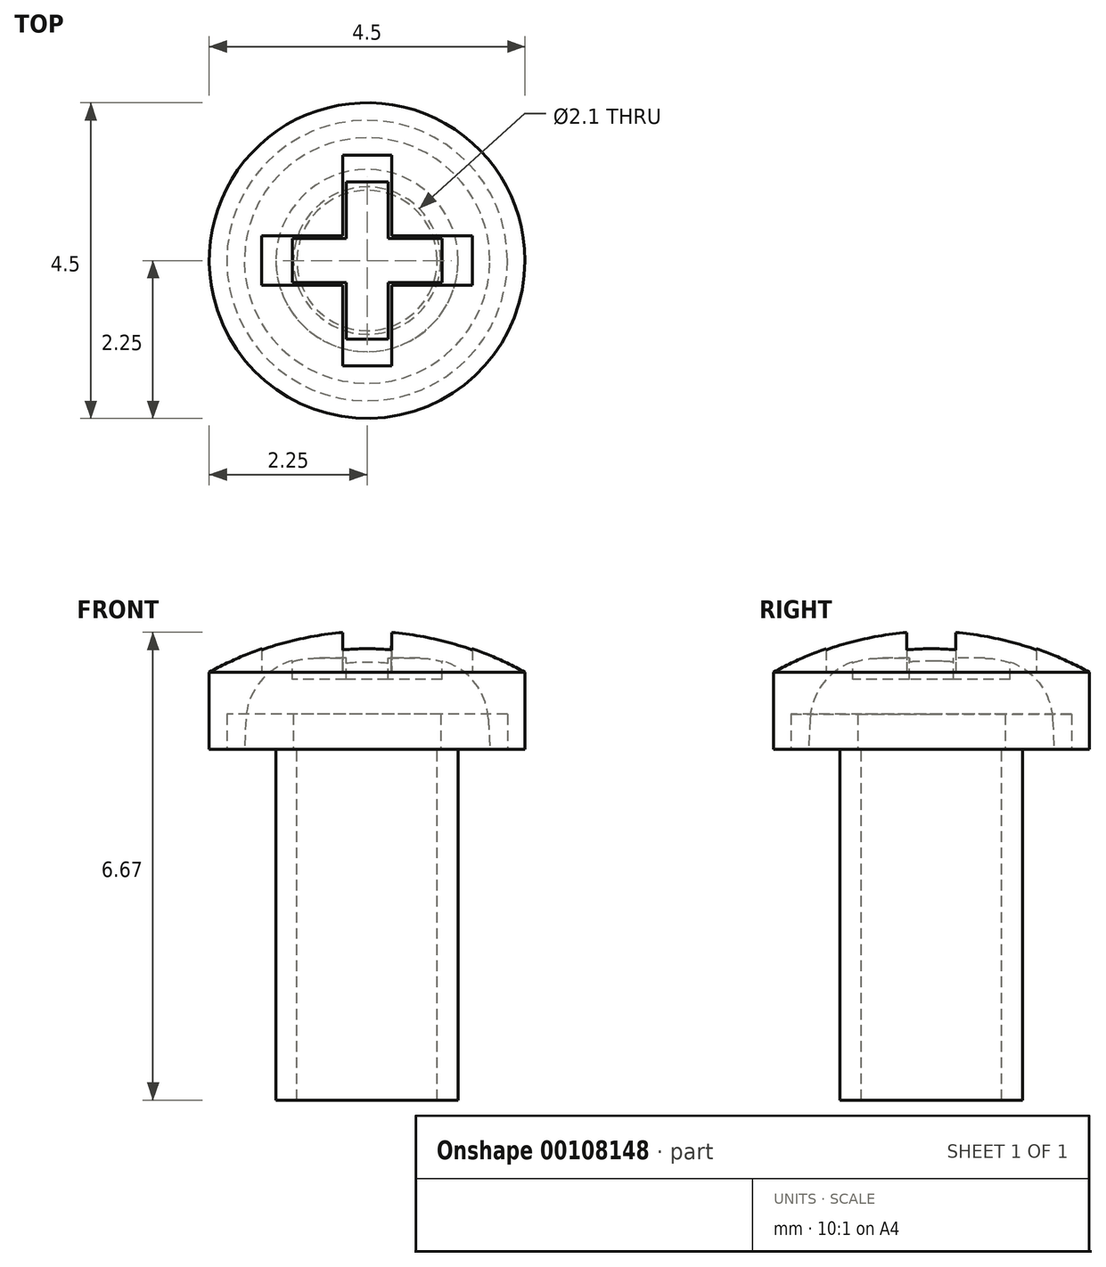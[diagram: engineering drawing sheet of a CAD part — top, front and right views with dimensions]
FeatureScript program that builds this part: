
annotation { "Feature Type Name" : "Feature", "Feature Type Description" : "" }
export const myFeature = defineFeature(function(context is Context, id is Id, definition is map)
    precondition{}
    {
        {
            var Q0;
            Q0=qCreatedBy(makeId("Front.planeOp"),FACE);
            var sketch = newSketch(context, id + "F0", { "sketchPlane" : qUnion([Q0])});
            skLineSegment(sketch, "E0", {"start": v(0, 1.5) * mm, "end": v(0, 0) * mm});
            skLineSegment(sketch, "E1", {"start": v(0, 0) * mm, "end": v(2, 0) * mm});
            skLineSegment(sketch, "E2", {"start": v(2, 0) * mm, "end": v(2, 0.7) * mm});
            skArc(sketch, "E3", {"start": v(2, 0.7) * mm, "mid": v(1.09, 1.31) * mm, "end": v(0, 1.5) * mm});
            skSolve(sketch);
        }
        {
            var Q0;
            Q0=qSketchRegion(id+"F0",true);
            var Q1;
            Q1=sQuery(id+"F0.wireOp",EDGE,"E0");
            revolve(context, id + "F1", {"entities" : qUnion([Q0]), "axis" : qUnion([Q1]), "revolveType" : RevolveType.FULL});
        }
        {
            var Q0;
            Q0=qCreatedBy(makeId("Top.planeOp"),FACE);
            cPlane(context, id + "F2", {"entities" : qUnion([Q0]), "cplaneType" : CPlaneType.OFFSET, "offset" : 1 * mm, "width" : 150 * mm, "height" : 150 * mm});
        }
        {
            var Q0;
            Q0=qCreatedBy(id+"F2.planeOp",FACE);
            var sketch = newSketch(context, id + "F3", { "sketchPlane" : qUnion([Q0])});
            skLineSegment(sketch, "E4.rect.bottom", {"start": v(0.34, 1.34) * mm, "end": v(-0.34, 1.34) * mm});
            skLineSegment(sketch, "E4.rect.top", {"start": v(0.34, -1.34) * mm, "end": v(-0.34, -1.34) * mm});
            skLineSegment(sketch, "E4.rect.left", {"start": v(0.34, 1.34) * mm, "end": v(0.34, -1.34) * mm});
            skLineSegment(sketch, "E4.rect.right", {"start": v(-0.34, 1.34) * mm, "end": v(-0.34, -1.34) * mm});
            skPoint(sketch, "E4.rect.middle", {"position": v(0, 0) * mm});
            skLineSegment(sketch, "E5.rect.bottom", {"start": v(1.32, 0.3) * mm, "end": v(-1.32, 0.3) * mm});
            skLineSegment(sketch, "E5.rect.top", {"start": v(1.32, -0.3) * mm, "end": v(-1.32, -0.3) * mm});
            skLineSegment(sketch, "E5.rect.left", {"start": v(1.32, 0.3) * mm, "end": v(1.32, -0.3) * mm});
            skLineSegment(sketch, "E5.rect.right", {"start": v(-1.32, 0.3) * mm, "end": v(-1.32, -0.3) * mm});
            skSolve(sketch);
        }
        {
            var Q0;
            Q0=qSketchRegion(id+"F3",true);
            extrude(context, id + "F4", {"entities" : qUnion([Q0]), "operationType" : NewBodyOperationType.REMOVE, "depth" : 25 * mm});
        }
        {
            var Q0;
            Q0=makeQuery(id+"F1.opRevolve","SWEPT_BODY",BODY,{"disambiguationData":[OSD([sQuery(id+"F0.wireOp",EDGE,"E0"),sQuery(id+"F0.wireOp",EDGE,"E1"),sQuery(id+"F0.wireOp",EDGE,"E2"),sQuery(id+"F0.wireOp",EDGE,"E3")])]});
            transform(context, id + "F5", {"entities" : qUnion([Q0]), "transformType" : TransformType.COPY});
        }
        {
            var Q0;
            Q0=makeQuery(id+"F1.opRevolve","SWEPT_FACE",FACE,{"disambiguationData":[OSD([sQuery(id+"F0.wireOp",EDGE,"E1")])]});
            var sketch = newSketch(context, id + "F6", { "sketchPlane" : qUnion([Q0])});
            skCircle(sketch, "E6", {"center": v(0, 0) * mm, "radius": 1.15 * mm});
            skSolve(sketch);
        }
        {
            var Q0;
            Q0=qSketchRegion(id+"F6",true);
            extrude(context, id + "F7", {"entities" : qUnion([Q0]), "operationType" : NewBodyOperationType.ADD, "depth" : 5 * mm});
        }
        {
            var Q0;
            Q0=qSketchRegion(id+"F6",true);
            extrude(context, id + "F8", {"entities" : qUnion([Q0]), "operationType" : NewBodyOperationType.ADD, "depth" : 4 * mm});
        }
        {
            var Q0;
            Q0=qCreatedBy(makeId("Front.planeOp"),FACE);
            var sketch = newSketch(context, id + "F9", { "sketchPlane" : qUnion([Q0])});
            skLineSegment(sketch, "E7", {"start": v(0, 0) * mm, "end": v(2.25, 0) * mm});
            skLineSegment(sketch, "E8", {"start": v(2.25, 0) * mm, "end": v(2.25, 1.1) * mm});
            skArc(sketch, "E9", {"start": v(2.25, 1.1) * mm, "mid": v(1.16, 1.54) * mm, "end": v(0, 1.7) * mm});
            skLineSegment(sketch, "E10", {"start": v(0, 1.7) * mm, "end": v(0, 0) * mm});
            skSolve(sketch);
        }
        {
            var Q0;
            Q0=qSketchRegion(id+"F9",true);
            var Q1;
            Q1=sQuery(id+"F9.wireOp",EDGE,"E10");
            revolve(context, id + "F10", {"entities" : qUnion([Q0]), "axis" : qUnion([Q1]), "revolveType" : RevolveType.FULL});
        }
        {
            var Q0;
            Q0=makeQuery(id+"F10.opRevolve","SWEPT_FACE",FACE,{"disambiguationData":[OSD([sQuery(id+"F9.wireOp",EDGE,"E7")])]});
            cPlane(context, id + "F11", {"entities" : qUnion([Q0]), "cplaneType" : CPlaneType.OFFSET, "offset" : 1.1 * mm, "oppositeDirection" : true, "width" : 150 * mm, "height" : 150 * mm});
        }
        {
            var Q0;
            Q0=qCreatedBy(id+"F11.planeOp",FACE);
            var sketch = newSketch(context, id + "F12", { "sketchPlane" : qUnion([Q0])});
            skLineSegment(sketch, "E11.rect.bottom", {"start": v(0.35, -1.5) * mm, "end": v(-0.35, -1.5) * mm});
            skLineSegment(sketch, "E11.rect.top", {"start": v(0.35, 1.5) * mm, "end": v(-0.35, 1.5) * mm});
            skLineSegment(sketch, "E11.rect.left", {"start": v(0.35, -1.5) * mm, "end": v(0.35, 1.5) * mm});
            skLineSegment(sketch, "E11.rect.right", {"start": v(-0.35, -1.5) * mm, "end": v(-0.35, 1.5) * mm});
            skPoint(sketch, "E11.rect.middle", {"position": v(0, 0) * mm});
            skLineSegment(sketch, "E12.rect.bottom", {"start": v(1.5, -0.35) * mm, "end": v(-1.5, -0.35) * mm});
            skLineSegment(sketch, "E12.rect.top", {"start": v(1.5, 0.35) * mm, "end": v(-1.5, 0.35) * mm});
            skLineSegment(sketch, "E12.rect.left", {"start": v(1.5, -0.35) * mm, "end": v(1.5, 0.35) * mm});
            skLineSegment(sketch, "E12.rect.right", {"start": v(-1.5, -0.35) * mm, "end": v(-1.5, 0.35) * mm});
            skSolve(sketch);
        }
        {
            var Q0;
            Q0=qSketchRegion(id+"F12",true);
            extrude(context, id + "F13", {"entities" : qUnion([Q0]), "operationType" : NewBodyOperationType.REMOVE, "oppositeDirection" : true, "depth" : 25 * mm});
        }
        {
            var Q0;
            Q0=makeQuery(id+"F10.opRevolve","SWEPT_BODY",BODY,{"disambiguationData":[OSD([sQuery(id+"F9.wireOp",EDGE,"E7"),sQuery(id+"F9.wireOp",EDGE,"E8"),sQuery(id+"F9.wireOp",EDGE,"E9"),sQuery(id+"F9.wireOp",EDGE,"E10")])]});
            transform(context, id + "F14", {"entities" : qUnion([Q0]), "transformType" : TransformType.COPY});
        }
        {
            var Q0;
            Q0=makeQuery(id+"F10.opRevolve","SWEPT_FACE",FACE,{"disambiguationData":[OSD([sQuery(id+"F9.wireOp",EDGE,"E7")])]});
            var sketch = newSketch(context, id + "F15", { "sketchPlane" : qUnion([Q0])});
            skCircle(sketch, "E13", {"center": v(0, 0) * mm, "radius": 1.3 * mm});
            skSolve(sketch);
        }
        {
            var Q0;
            Q0=qSketchRegion(id+"F15",true);
            extrude(context, id + "F16", {"entities" : qUnion([Q0]), "operationType" : NewBodyOperationType.ADD, "depth" : 4 * mm});
        }
        {
            var Q0;
            Q0=qSketchRegion(id+"F15",true);
            extrude(context, id + "F17", {"entities" : qUnion([Q0]), "operationType" : NewBodyOperationType.ADD, "depth" : 5 * mm});
        }
        {
            var Q0;
            Q0=qCreatedBy(makeId("Front.planeOp"),FACE);
            var sketch = newSketch(context, id + "F18", { "sketchPlane" : qUnion([Q0])});
            skLineSegment(sketch, "E14", {"start": v(0, 0) * mm, "end": v(1.75, 0) * mm});
            skLineSegment(sketch, "E15", {"start": v(0, 1.3) * mm, "end": v(0, 0) * mm});
            skLineSegment(sketch, "E16", {"start": v(0, 1.3) * mm, "end": v(0.82, 1.3) * mm});
            skLineSegment(sketch, "E17", {"start": v(1.75, 0) * mm, "end": v(1.73, 0.43) * mm});
            skArc(sketch, "E18", {"start": v(1.73, 0.43) * mm, "mid": v(1.45, 1.05) * mm, "end": v(0.82, 1.3) * mm});
            skLineSegment(sketch, "E19.bottom", {"start": v(0, 0) * mm, "end": v(1, 0) * mm});
            skLineSegment(sketch, "E19.top", {"start": v(0, -5) * mm, "end": v(1, -5) * mm});
            skLineSegment(sketch, "E19.left", {"start": v(0, 0) * mm, "end": v(0, -5) * mm});
            skLineSegment(sketch, "E19.right", {"start": v(1, 0) * mm, "end": v(1, -5) * mm});
            skSolve(sketch);
        }
        {
            var Q0;
            Q0=qSketchRegion(id+"F18",true);
            var Q1;
            Q1=sQuery(id+"F18.wireOp",EDGE,"E19.left");
            revolve(context, id + "F19", {"entities" : qUnion([Q0]), "axis" : qUnion([Q1]), "revolveType" : RevolveType.FULL});
        }
        {
            var Q0;
            Q0=makeQuery(id+"F19.opRevolve","SWEPT_FACE",FACE,{"disambiguationData":[OSD([sQuery(id+"F18.wireOp",EDGE,"E16")])]});
            var sketch = newSketch(context, id + "F20", { "sketchPlane" : qUnion([Q0])});
            skLineSegment(sketch, "E20.bottom", {"start": v(0.3, 1.12) * mm, "end": v(-0.3, 1.12) * mm});
            skLineSegment(sketch, "E20.top", {"start": v(0.3, -1.12) * mm, "end": v(-0.3, -1.12) * mm});
            skLineSegment(sketch, "E20.left", {"start": v(0.3, 1.12) * mm, "end": v(0.3, -1.12) * mm});
            skLineSegment(sketch, "E20.right", {"start": v(-0.3, 1.12) * mm, "end": v(-0.3, -1.12) * mm});
            skPoint(sketch, "E20.middle", {"position": v(0, 0) * mm});
            skLineSegment(sketch, "E21.bottom", {"start": v(1.07, 0.31) * mm, "end": v(-1.07, 0.31) * mm});
            skLineSegment(sketch, "E21.top", {"start": v(1.07, -0.31) * mm, "end": v(-1.07, -0.31) * mm});
            skLineSegment(sketch, "E21.left", {"start": v(1.07, 0.31) * mm, "end": v(1.07, -0.31) * mm});
            skLineSegment(sketch, "E21.right", {"start": v(-1.07, 0.31) * mm, "end": v(-1.07, -0.31) * mm});
            skSolve(sketch);
        }
        {
            var Q0;
            Q0=qSketchRegion(id+"F20",true);
            extrude(context, id + "F21", {"entities" : qUnion([Q0]), "operationType" : NewBodyOperationType.REMOVE, "oppositeDirection" : true, "depth" : 0.3 * mm});
        }
        {
            var Q0;
            Q0=qCreatedBy(makeId("Top.planeOp"),FACE);
            var sketch = newSketch(context, id + "F22", { "sketchPlane" : qUnion([Q0])});
            skCircle(sketch, "E22", {"center": v(0, 0) * mm, "radius": 2 * mm});
            skCircle(sketch, "E23", {"center": v(0, 0) * mm, "radius": 1.05 * mm});
            skSolve(sketch);
        }
        {
            var Q0;
            Q0=qSketchRegion(id+"F22",true);
            extrude(context, id + "F23", {"entities" : qUnion([Q0]), "depth" : 0.5 * mm});
        }
    });
